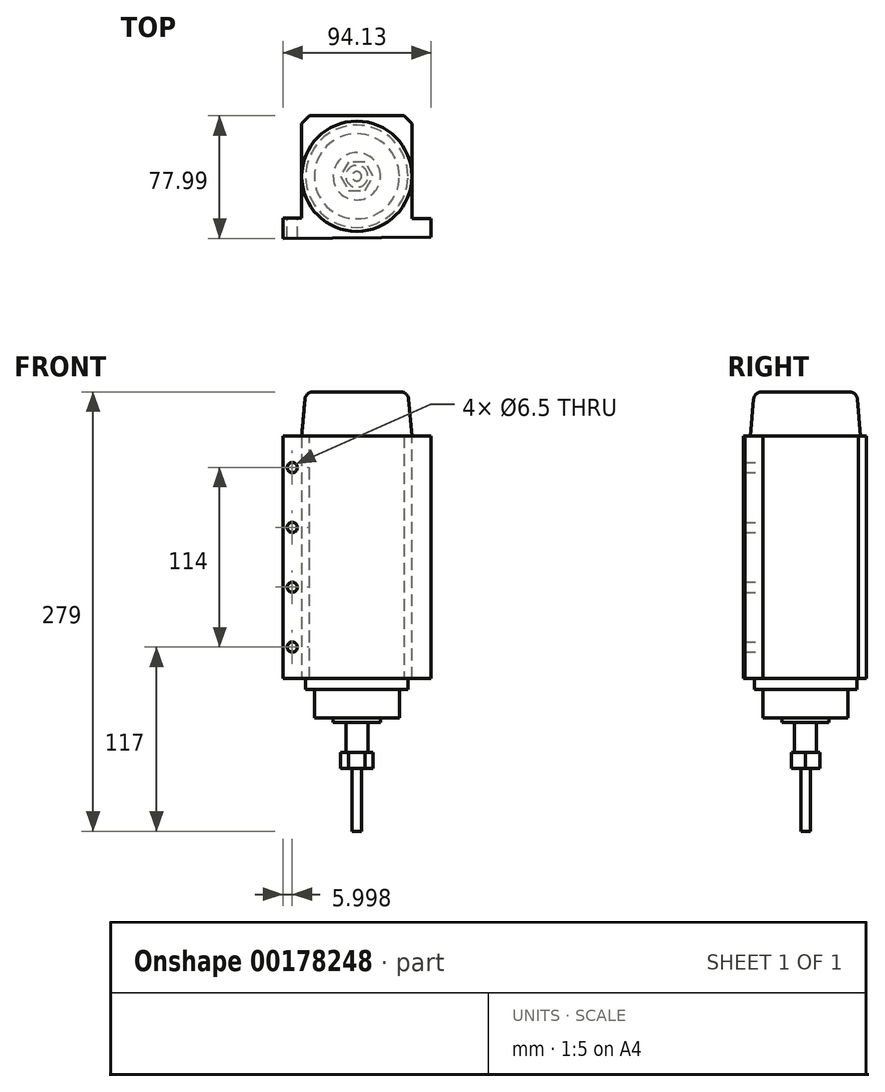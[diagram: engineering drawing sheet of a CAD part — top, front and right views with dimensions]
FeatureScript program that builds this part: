
annotation { "Feature Type Name" : "Feature", "Feature Type Description" : "" }
export const myFeature = defineFeature(function(context is Context, id is Id, definition is map)
    precondition{}
    {
        {
            var Q0;
            Q0=qCreatedBy(makeId("Top.planeOp"),FACE);
            var sketch = newSketch(context, id + "F0", { "sketchPlane" : qUnion([Q0])});
            skLineSegment(sketch, "E0.top", {"start": v(35, 38.5) * mm, "end": v(-35, 38.5) * mm});
            skLineSegment(sketch, "E0.left", {"start": v(35, -27) * mm, "end": v(35, 38.5) * mm});
            skLineSegment(sketch, "E0.right", {"start": v(-35, -26.68) * mm, "end": v(-35, 38.5) * mm});
            skPoint(sketch, "E0.middle", {"position": v(0, 0) * mm});
            skLineSegment(sketch, "E1.top", {"start": v(-35, -26.68) * mm, "end": v(-47, -26.68) * mm});
            skLineSegment(sketch, "E1.right", {"start": v(-46.87, -39.49) * mm, "end": v(-47, -26.68) * mm});
            skLineSegment(sketch, "E2.top", {"start": v(35, -27) * mm, "end": v(47, -27) * mm});
            skLineSegment(sketch, "E2.right", {"start": v(47.13, -38.5) * mm, "end": v(47, -27) * mm});
            skLineSegment(sketch, "E3", {"start": v(-46.87, -39.49) * mm, "end": v(47.13, -38.5) * mm});
            skSolve(sketch);
        }
        {
            var Q0;
            Q0=makeQuery(id+"F0.imprint","IMPRINT",FACE,{"disambiguationData":[TD([[makeQuery(id+"F0.imprint","IMPRINT",EDGE,{"derivedFrom":sQuery(id+"F0.wireOp",EDGE,"E0.top")}),1.0]])]});
            extrude(context, id + "F1", {"entities" : qUnion([Q0]), "depth" : 154 * mm});
        }
        {
            var Q0;
            Q0=makeQuery(id+"F1.opExtrude","CAP_FACE",FACE,{"disambiguationData":[OSD([sQuery(id+"F0.wireOp",EDGE,"E0.top"),sQuery(id+"F0.wireOp",EDGE,"E0.left"),sQuery(id+"F0.wireOp",EDGE,"E0.right"),sQuery(id+"F0.wireOp",EDGE,"E1.top"),sQuery(id+"F0.wireOp",EDGE,"E1.right"),sQuery(id+"F0.wireOp",EDGE,"E2.top"),sQuery(id+"F0.wireOp",EDGE,"E2.right"),sQuery(id+"F0.wireOp",EDGE,"E3")])],"isStart":false});
            var sketch = newSketch(context, id + "F2", { "sketchPlane" : qUnion([Q0])});
            skLineSegment(sketch, "E4", {"start": v(0, 38.5) * mm, "end": v(0, -39) * mm, "construction": true});
            skPoint(sketch, "E5", {"position": v(0, 0) * mm});
            skCircle(sketch, "E6", {"center": v(0, 0) * mm, "radius": 35 * mm});
            skSolve(sketch);
        }
        {
            var Q0;
            Q0=qSketchRegion(id+"F2",true);
            extrude(context, id + "F3", {"entities" : qUnion([Q0]), "operationType" : NewBodyOperationType.ADD, "depth" : 28 * mm, "hasDraft" : true, "draftAngle" : 5 * degree, "draftPullDirection" : true});
        }
        {
            var Q0;
            Q0=makeQuery(id+"F3.opExtrude","CAP_EDGE",EDGE,{"disambiguationData":[OSD([sQuery(id+"F2.wireOp",EDGE,"E6")])],"isStart":false});
            fillet(context, id + "F4", {"entities" : qUnion([Q0]), "radius" : 5 * mm, "tangentPropagation" : true, "allowEdgeOverflow" : false});
        }
        {
            var Q0;
            Q0=makeQuery(id+"F1.opExtrude","CAP_FACE",FACE,{"disambiguationData":[OSD([sQuery(id+"F0.wireOp",EDGE,"E0.top"),sQuery(id+"F0.wireOp",EDGE,"E0.left"),sQuery(id+"F0.wireOp",EDGE,"E0.right"),sQuery(id+"F0.wireOp",EDGE,"E1.top"),sQuery(id+"F0.wireOp",EDGE,"E1.right"),sQuery(id+"F0.wireOp",EDGE,"E2.top"),sQuery(id+"F0.wireOp",EDGE,"E2.right"),sQuery(id+"F0.wireOp",EDGE,"E3")])],"isStart":true});
            var sketch = newSketch(context, id + "F5", { "sketchPlane" : qUnion([Q0])});
            skCircle(sketch, "E7", {"center": v(0, 0) * mm, "radius": 32.5 * mm});
            skSolve(sketch);
        }
        {
            var Q0;
            Q0=qSketchRegion(id+"F5",true);
            extrude(context, id + "F6", {"entities" : qUnion([Q0]), "operationType" : NewBodyOperationType.ADD, "depth" : 7 * mm});
        }
        {
            var Q0;
            Q0=makeQuery(id+"F6.opExtrude","CAP_FACE",FACE,{"disambiguationData":[OSD([sQuery(id+"F5.wireOp",EDGE,"E7")])],"isStart":false});
            var sketch = newSketch(context, id + "F7", { "sketchPlane" : qUnion([Q0])});
            skCircle(sketch, "E8", {"center": v(0, 0) * mm, "radius": 27 * mm});
            skSolve(sketch);
        }
        {
            var Q0;
            Q0=qSketchRegion(id+"F7",true);
            extrude(context, id + "F8", {"entities" : qUnion([Q0]), "operationType" : NewBodyOperationType.ADD, "depth" : 18 * mm});
        }
        {
            var Q0;
            Q0=makeQuery(id+"F8.opExtrude","CAP_FACE",FACE,{"disambiguationData":[OSD([sQuery(id+"F7.wireOp",EDGE,"E8")])],"isStart":false});
            var sketch = newSketch(context, id + "F9", { "sketchPlane" : qUnion([Q0])});
            skCircle(sketch, "E9", {"center": v(0, 0) * mm, "radius": 7 * mm});
            skCircle(sketch, "E10", {"center": v(0, 0) * mm, "radius": 15 * mm});
            skSolve(sketch);
        }
        {
            var Q0;
            Q0=makeQuery(id+"F9.imprint","IMPRINT",FACE,{"disambiguationData":[TD([[makeQuery(id+"F9.imprint","IMPRINT",EDGE,{"derivedFrom":sQuery(id+"F9.wireOp",EDGE,"E9")}),1.0]])]});
            extrude(context, id + "F10", {"entities" : qUnion([Q0]), "operationType" : NewBodyOperationType.ADD, "depth" : 32 * mm});
        }
        {
            var Q0;
            Q0=makeQuery(id+"F9.imprint","IMPRINT",FACE,{"disambiguationData":[TD([[makeQuery(id+"F9.imprint","IMPRINT",EDGE,{"derivedFrom":sQuery(id+"F9.wireOp",EDGE,"E9")}),-1.0]])]});
            extrude(context, id + "F11", {"entities" : qUnion([Q0]), "operationType" : NewBodyOperationType.ADD, "depth" : 3 * mm});
        }
        {
            var Q0;
            Q0=makeQuery(id+"F10.opExtrude","CAP_FACE",FACE,{"disambiguationData":[OSD([sQuery(id+"F9.wireOp",EDGE,"E9")])],"isStart":false});
            var sketch = newSketch(context, id + "F12", { "sketchPlane" : qUnion([Q0])});
            skCircle(sketch, "E11.cCircle", {"center": v(0, 0) * mm, "radius": 9.03 * mm, "construction": true});
            skLineSegment(sketch, "E11.0", {"start": v(-5.21, 9.03) * mm, "end": v(5.21, 9.03) * mm});
            skLineSegment(sketch, "E11.1", {"start": v(5.21, 9.03) * mm, "end": v(10.43, 0) * mm});
            skLineSegment(sketch, "E11.2", {"start": v(10.43, 0) * mm, "end": v(5.21, -9.03) * mm});
            skLineSegment(sketch, "E11.3", {"start": v(5.21, -9.03) * mm, "end": v(-5.21, -9.03) * mm});
            skLineSegment(sketch, "E11.4", {"start": v(-5.21, -9.03) * mm, "end": v(-10.43, 0) * mm});
            skLineSegment(sketch, "E11.5", {"start": v(-10.43, 0) * mm, "end": v(-5.21, 9.03) * mm});
            skPoint(sketch, "E11.0.midPoint", {"position": v(0, 9.03) * mm});
            skSolve(sketch);
        }
        {
            var Q0;
            Q0=qSketchRegion(id+"F12",true);
            extrude(context, id + "F13", {"entities" : qUnion([Q0]), "operationType" : NewBodyOperationType.ADD, "oppositeDirection" : true, "depth" : 10 * mm});
        }
        {
            var Q0;
            Q0=makeQuery(id+"F13.boolean.opBoolean","MERGE",FACE,{"derivedFrom":[makeQuery(id+"F10.opExtrude","CAP_FACE",FACE,{"disambiguationData":[OSD([sQuery(id+"F9.wireOp",EDGE,"E9")])],"isStart":false}),makeQuery(id+"F13.opExtrude","CAP_FACE",FACE,{"disambiguationData":[OSD([sQuery(id+"F12.wireOp",EDGE,"E11.0"),sQuery(id+"F12.wireOp",EDGE,"E11.1"),sQuery(id+"F12.wireOp",EDGE,"E11.2"),sQuery(id+"F12.wireOp",EDGE,"E11.3"),sQuery(id+"F12.wireOp",EDGE,"E11.4"),sQuery(id+"F12.wireOp",EDGE,"E11.5")])],"isStart":true})]});
            var sketch = newSketch(context, id + "F14", { "sketchPlane" : qUnion([Q0])});
            skCircle(sketch, "E12", {"center": v(0, 0) * mm, "radius": 3 * mm});
            skSolve(sketch);
        }
        {
            var Q0;
            Q0=qSketchRegion(id+"F14",true);
            extrude(context, id + "F15", {"entities" : qUnion([Q0]), "operationType" : NewBodyOperationType.ADD, "depth" : 40 * mm});
        }
        {
            var Q0;
            Q0=makeQuery(id+"F1.opExtrude","SWEPT_EDGE",EDGE,{"disambiguationData":[OSD([sQuery(id+"F0.wireOp",EDGE,"E0.top"),sQuery(id+"F0.wireOp",EDGE,"E0.left")])]});
            var Q1;
            Q1=makeQuery(id+"F1.opExtrude","SWEPT_EDGE",EDGE,{"disambiguationData":[OSD([sQuery(id+"F0.wireOp",EDGE,"E0.top"),sQuery(id+"F0.wireOp",EDGE,"E0.right")])]});
            chamfer(context, id + "F16", {"entities" : qUnion([Q0, Q1]), "width" : 5 * mm, "tangentPropagation" : true});
        }
        {
            var Q0;
            Q0=makeQuery(id+"F1.opExtrude","SWEPT_FACE",FACE,{"disambiguationData":[OSD([sQuery(id+"F0.wireOp",EDGE,"E1.top")])]});
            var sketch = newSketch(context, id + "F17", { "sketchPlane" : qUnion([Q0])});
            skLineSegment(sketch, "E13", {"start": v(41, 0) * mm, "end": v(41, 154) * mm, "construction": true});
            skLineSegment(sketch, "E14", {"start": v(47, 20) * mm, "end": v(35, 20) * mm, "construction": true});
            skLineSegment(sketch, "E15", {"start": v(47, 58) * mm, "end": v(35, 58) * mm, "construction": true});
            skPoint(sketch, "E15.endSnap0", {"position": v(35, 77) * mm});
            skLineSegment(sketch, "E16", {"start": v(47, 96) * mm, "end": v(35, 96) * mm, "construction": true});
            skLineSegment(sketch, "E17", {"start": v(47, 134) * mm, "end": v(35, 134) * mm, "construction": true});
            skPoint(sketch, "E18", {"position": v(41, 20) * mm});
            skPoint(sketch, "E19", {"position": v(41, 58) * mm});
            skPoint(sketch, "E20", {"position": v(41, 96) * mm});
            skPoint(sketch, "E21", {"position": v(41, 134) * mm});
            skLineSegment(sketch, "E22", {"start": v(0, 8.24) * mm, "end": v(0, 72.92) * mm, "construction": true});
            skSolve(sketch);
        }
        {
            var Q0;
            Q0=sQuery(id+"F17.wireOp",VERTEX,"E18");
            var Q1;
            Q1=sQuery(id+"F17.wireOp",VERTEX,"E19");
            var Q2;
            Q2=sQuery(id+"F17.wireOp",VERTEX,"E20");
            var Q3;
            Q3=sQuery(id+"F17.wireOp",VERTEX,"E21");
            var Q4;
            Q4=makeQuery(id+"F1.opExtrude","SWEPT_BODY",BODY,{"disambiguationData":[OSD([sQuery(id+"F0.wireOp",EDGE,"E0.top"),sQuery(id+"F0.wireOp",EDGE,"E0.left"),sQuery(id+"F0.wireOp",EDGE,"E0.right"),sQuery(id+"F0.wireOp",EDGE,"E1.top"),sQuery(id+"F0.wireOp",EDGE,"E1.right"),sQuery(id+"F0.wireOp",EDGE,"E2.top"),sQuery(id+"F0.wireOp",EDGE,"E2.right"),sQuery(id+"F0.wireOp",EDGE,"E3")])]});
            hole(context, id + "F18", {"style" : HoleStyle.SIMPLE, "endStyle" : HoleEndStyle.THROUGH, "holeDiameter" : 6.5 * mm, "locations" : qUnion([Q0, Q1, Q2, Q3]), "scope" : qUnion([Q4]), "isTappedThrough" : true});
        }
    });
